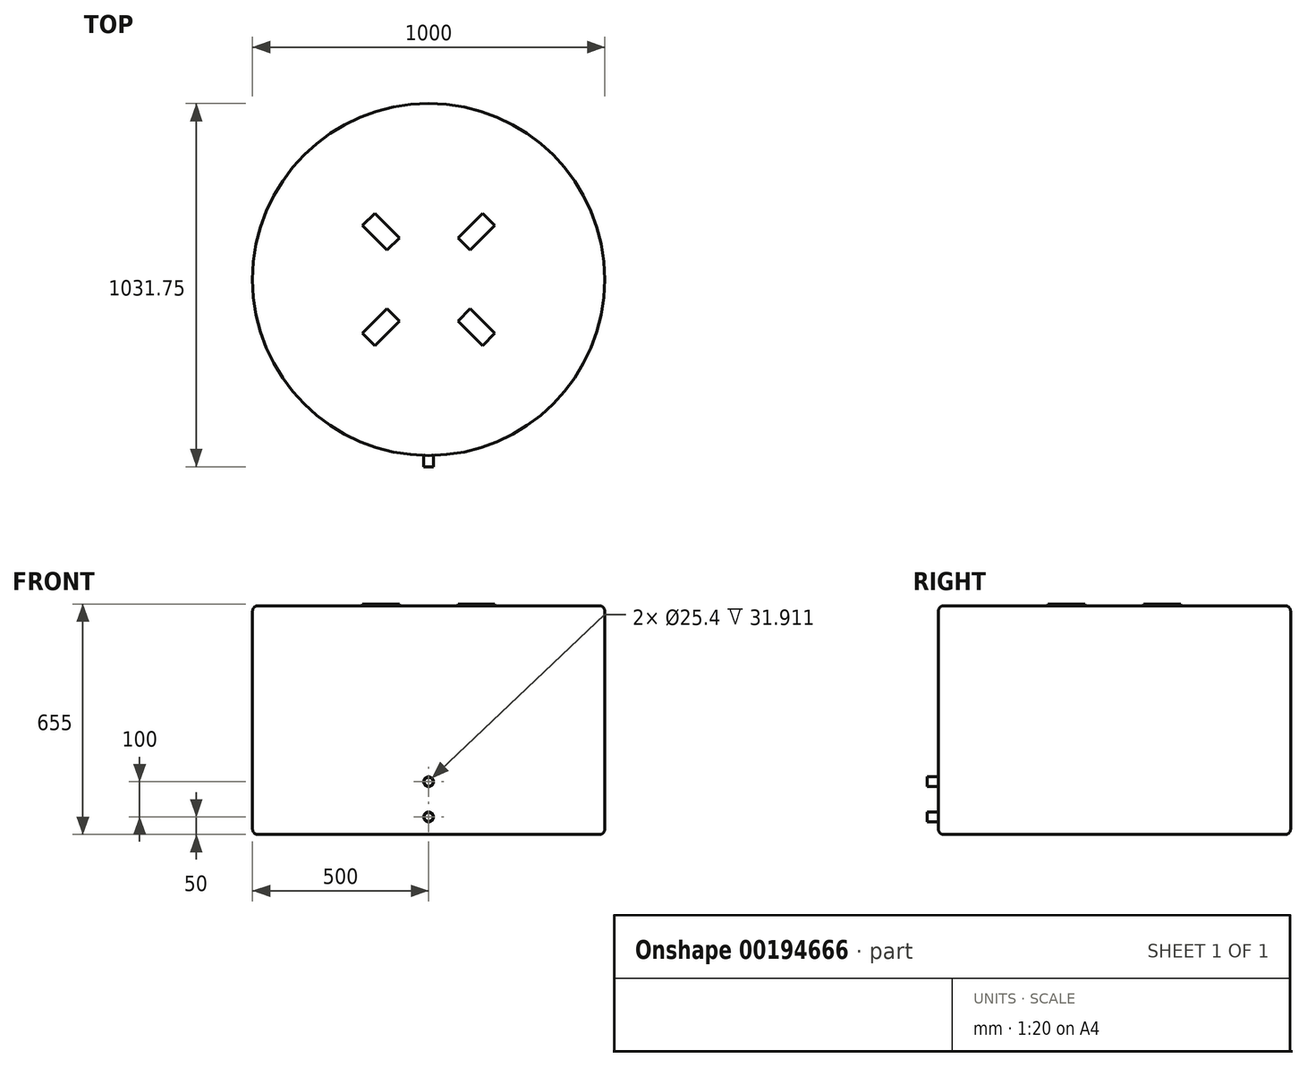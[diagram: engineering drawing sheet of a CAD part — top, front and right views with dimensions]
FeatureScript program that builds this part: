
annotation { "Feature Type Name" : "Feature", "Feature Type Description" : "" }
export const myFeature = defineFeature(function(context is Context, id is Id, definition is map)
    precondition{}
    {
        {
            var Q0;
            Q0=qCreatedBy(makeId("Top.planeOp"),FACE);
            var sketch = newSketch(context, id + "F0", { "sketchPlane" : qUnion([Q0])});
            skCircle(sketch, "E0", {"center": v(0, 0) * mm, "radius": 500 * mm});
            skSolve(sketch);
        }
        {
            var Q0;
            Q0 = qSketchRegion(id + "F0", true);
            extrude(context, id + "F1", {"entities" : qUnion([Q0]), "oppositeDirection" : true, "depth" : 650 * mm});
        }
        {
            var Q0;
            Q0=makeQuery(id+"F1.opExtrude","CAP_EDGE",EDGE,{"disambiguationData":[OSD([sQuery(id+"F0.wireOp",EDGE,"E0")])],"isStart":true});
            fillet(context, id + "F2", {"entities" : qUnion([Q0]), "radius" : 15 * mm, "tangentPropagation" : true, "allowEdgeOverflow" : false});
        }
        {
            var Q0;
            Q0=makeQuery(id+"F1.opExtrude","CAP_EDGE",EDGE,{"disambiguationData":[OSD([sQuery(id+"F0.wireOp",EDGE,"E0")])],"isStart":false});
            fillet(context, id + "F3", {"entities" : qUnion([Q0]), "radius" : 15 * mm, "tangentPropagation" : true, "allowEdgeOverflow" : false});
        }
        {
            var Q0;
            Q0=qCreatedBy(makeId("Front.planeOp"),FACE);
            cPlane(context, id + "F4", {"entities" : qUnion([Q0]), "cplaneType" : CPlaneType.OFFSET, "offset" : 500 * mm, "width" : 152.4 * mm, "height" : 152.4 * mm});
        }
        {
            var Q0;
            Q0=qCreatedBy(id+"F4.planeOp",FACE);
            var sketch = newSketch(context, id + "F5", { "sketchPlane" : qUnion([Q0])});
            skLineSegment(sketch, "E1", {"start": v(0, 0) * mm, "end": v(0, -633.78) * mm, "construction": true});
            skCircle(sketch, "E2", {"center": v(0, -600) * mm, "radius": 12.7 * mm});
            skCircle(sketch, "E3", {"center": v(0, -500) * mm, "radius": 12.7 * mm});
            skCircle(sketch, "E4", {"center": v(0, -500) * mm, "radius": 13.97 * mm});
            skCircle(sketch, "E5", {"center": v(0, -600) * mm, "radius": 13.97 * mm});
            skSolve(sketch);
        }
        {
            var Q0;
            Q0 = qSketchRegion(id + "F5", true);
            extrude(context, id + "F6", {"entities" : qUnion([Q0]), "operationType" : NewBodyOperationType.ADD, "endBound" : BoundingType.SYMMETRIC, "depth" : 63.5 * mm});
        }
        {
            var Q0;
            Q0=makeQuery(id+"F0.imprint","IMPRINT",FACE,{"disambiguationData":[TD([[makeQuery(id+"F0.imprint","IMPRINT",EDGE,{"derivedFrom":sQuery(id+"F0.wireOp",EDGE,"E0")}),1.0]])]});
            var sketch = newSketch(context, id + "F7", { "sketchPlane" : qUnion([Q0])});
            skLineSegment(sketch, "E6", {"start": v(-239.46, 239.46) * mm, "end": v(363.45, -363.45) * mm, "construction": true});
            skLineSegment(sketch, "E7", {"start": v(-272.9, -272.9) * mm, "end": v(100, 100) * mm, "construction": true});
            skLineSegment(sketch, "E8", {"start": v(-395.16, 0) * mm, "end": v(531.87, 0) * mm, "construction": true});
            skLineSegment(sketch, "E9.bottom", {"start": v(-100, -100) * mm, "end": v(100, -100) * mm, "construction": true});
            skLineSegment(sketch, "E9.top", {"start": v(-100, 100) * mm, "end": v(100, 100) * mm, "construction": true});
            skLineSegment(sketch, "E9.left", {"start": v(-100, -100) * mm, "end": v(-100, 100) * mm, "construction": true});
            skLineSegment(sketch, "E9.right", {"start": v(100, -100) * mm, "end": v(100, 100) * mm, "construction": true});
            skLineSegment(sketch, "E10", {"start": v(-82.32, 117.68) * mm, "end": v(-117.68, 82.32) * mm});
            skLineSegment(sketch, "E11.MirrorCS", {"start": v(117.68, -82.32) * mm, "end": v(82.32, -117.68) * mm});
            skLineSegment(sketch, "E12.MirrorCS", {"start": v(-82.32, -117.68) * mm, "end": v(-117.68, -82.32) * mm});
            skLineSegment(sketch, "E13.MirrorCS", {"start": v(117.68, 82.32) * mm, "end": v(82.32, 117.68) * mm});
            skLineSegment(sketch, "E14", {"start": v(-117.68, 82.32) * mm, "end": v(-188.39, 153.03) * mm});
            skLineSegment(sketch, "E15", {"start": v(-188.39, 153.03) * mm, "end": v(-153.03, 188.39) * mm});
            skLineSegment(sketch, "E16", {"start": v(-153.03, 188.39) * mm, "end": v(-82.32, 117.68) * mm});
            skLineSegment(sketch, "E17", {"start": v(-118.38, 83.03) * mm, "end": v(-83.03, 118.38) * mm});
            skLineSegment(sketch, "E18.MirrorCS", {"start": v(-153.03, -188.39) * mm, "end": v(-82.32, -117.68) * mm});
            skLineSegment(sketch, "E19.MirrorCS", {"start": v(-188.39, -153.03) * mm, "end": v(-153.03, -188.39) * mm});
            skLineSegment(sketch, "E20.MirrorCS", {"start": v(-117.68, -82.32) * mm, "end": v(-188.39, -153.03) * mm});
            skLineSegment(sketch, "E21.MirrorCS", {"start": v(-118.38, -83.03) * mm, "end": v(-83.03, -118.38) * mm});
            skLineSegment(sketch, "E22.MirrorCS", {"start": v(153.03, 188.39) * mm, "end": v(82.32, 117.68) * mm});
            skLineSegment(sketch, "E23.MirrorCS", {"start": v(188.39, 153.03) * mm, "end": v(153.03, 188.39) * mm});
            skLineSegment(sketch, "E24.MirrorCS", {"start": v(117.68, 82.32) * mm, "end": v(188.39, 153.03) * mm});
            skLineSegment(sketch, "E25.MirrorCS", {"start": v(117.68, -82.32) * mm, "end": v(188.39, -153.03) * mm});
            skLineSegment(sketch, "E26.MirrorCS", {"start": v(188.39, -153.03) * mm, "end": v(153.03, -188.39) * mm});
            skLineSegment(sketch, "E27.MirrorCS", {"start": v(153.03, -188.39) * mm, "end": v(82.32, -117.68) * mm});
            skLineSegment(sketch, "E28.MirrorCS", {"start": v(118.38, -83.03) * mm, "end": v(83.03, -118.38) * mm});
            skLineSegment(sketch, "E29.MirrorCS", {"start": v(118.38, 83.03) * mm, "end": v(83.03, 118.38) * mm});
            skLineSegment(sketch, "E30", {"start": v(-83.03, -118.38) * mm, "end": v(-82.32, -117.68) * mm});
            skLineSegment(sketch, "E31", {"start": v(-117.68, -82.32) * mm, "end": v(-118.38, -83.03) * mm});
            skLineSegment(sketch, "E32", {"start": v(-83.03, 118.38) * mm, "end": v(-82.32, 117.68) * mm});
            skLineSegment(sketch, "E33", {"start": v(-117.68, 82.32) * mm, "end": v(-118.38, 83.03) * mm});
            skSolve(sketch);
        }
        {
            var Q0;
            {var subQ0=sQuery(id+"F7.wireOp",EDGE,"E19.MirrorCS");Q0=makeQuery(id+"F7.imprint","IMPRINT",FACE,{"disambiguationData":[TD([[makeQuery(id+"F7.imprint","IMPRINT",EDGE,{"derivedFrom":subQ0}),1.0]])]});}
            var Q1;
            {var subQ0=sQuery(id+"F7.wireOp",EDGE,"E26.MirrorCS");Q1=makeQuery(id+"F7.imprint","IMPRINT",FACE,{"disambiguationData":[TD([[makeQuery(id+"F7.imprint","IMPRINT",EDGE,{"derivedFrom":subQ0}),-1.0]])]});}
            var Q2;
            {var subQ0=sQuery(id+"F7.wireOp",EDGE,"E15");Q2=makeQuery(id+"F7.imprint","IMPRINT",FACE,{"disambiguationData":[TD([[makeQuery(id+"F7.imprint","IMPRINT",EDGE,{"derivedFrom":subQ0}),-1.0]])]});}
            var Q3;
            {var subQ0=sQuery(id+"F7.wireOp",EDGE,"E23.MirrorCS");Q3=makeQuery(id+"F7.imprint","IMPRINT",FACE,{"disambiguationData":[TD([[makeQuery(id+"F7.imprint","IMPRINT",EDGE,{"derivedFrom":subQ0}),1.0]])]});}
            extrude(context, id + "F8", {"entities" : qUnion([Q0, Q1, Q2, Q3]), "operationType" : NewBodyOperationType.ADD, "depth" : 5 * mm});
        }
    });
